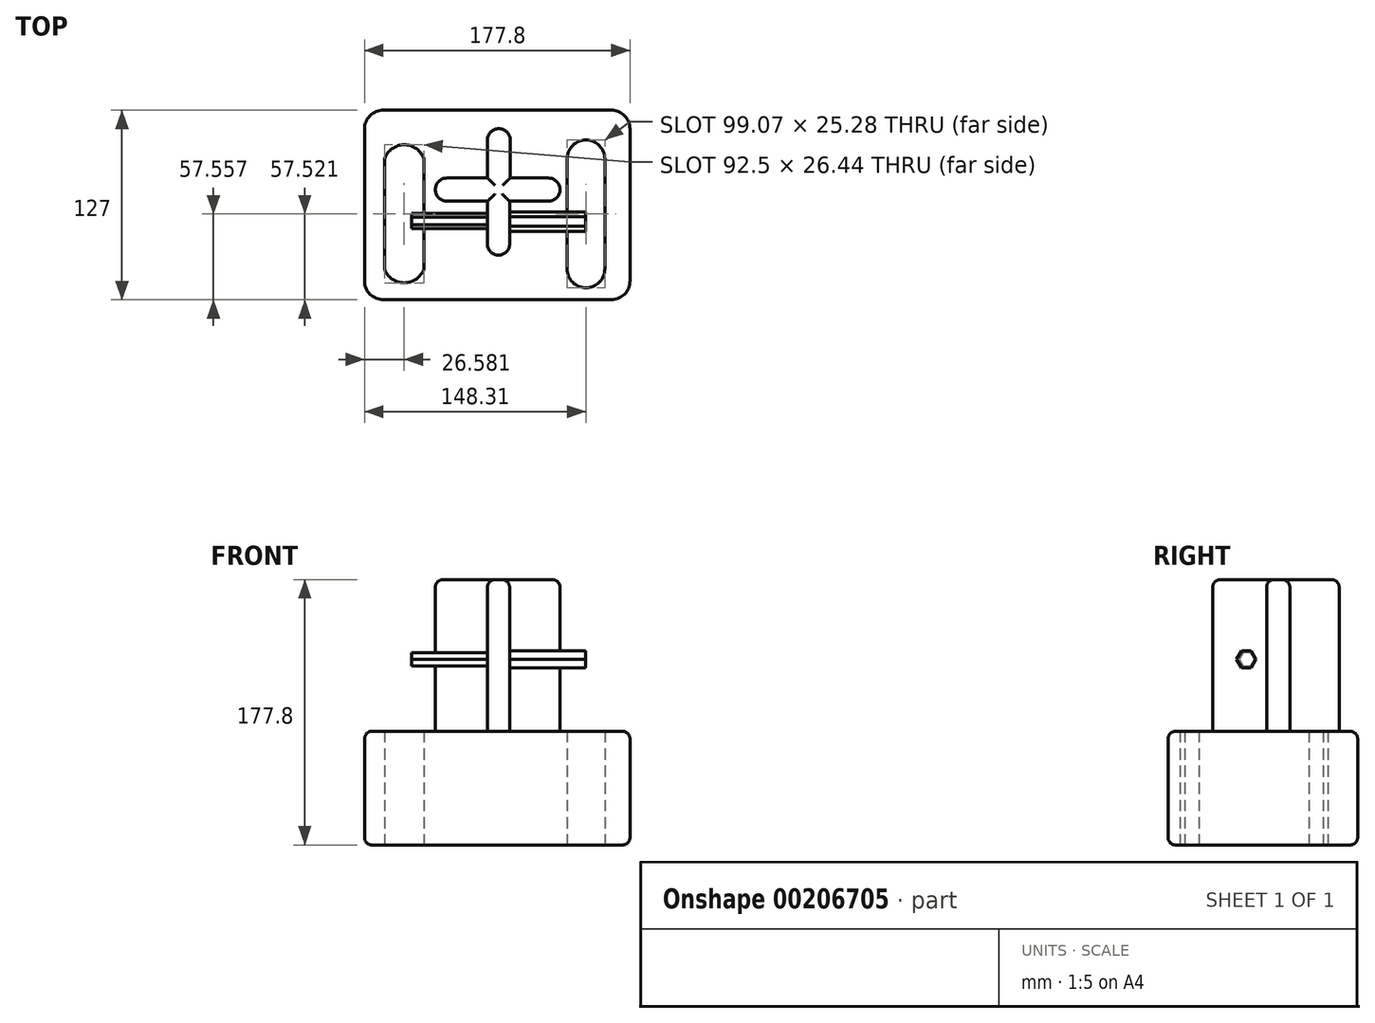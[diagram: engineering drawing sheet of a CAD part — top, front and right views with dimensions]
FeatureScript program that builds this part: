
annotation { "Feature Type Name" : "Feature", "Feature Type Description" : "" }
export const myFeature = defineFeature(function(context is Context, id is Id, definition is map)
    precondition{}
    {
        {
            var Q0;
            Q0=qCreatedBy(makeId("Top.planeOp"),FACE);
            var sketch = newSketch(context, id + "F0", { "sketchPlane" : qUnion([Q0])});
            skLineSegment(sketch, "E0", {"start": v(-97.17, 61.03) * mm, "end": v(-97.17, -65.97) * mm});
            skLineSegment(sketch, "E1", {"start": v(-97.17, -65.97) * mm, "end": v(80.63, -65.97) * mm});
            skLineSegment(sketch, "E2", {"start": v(80.63, -65.97) * mm, "end": v(80.63, 61.03) * mm});
            skLineSegment(sketch, "E3", {"start": v(80.63, 61.03) * mm, "end": v(-97.17, 61.03) * mm});
            skLineSegment(sketch, "E4", {"start": v(-83.8, 28.45) * mm, "end": v(-83.8, -45.35) * mm});
            skLineSegment(sketch, "E5", {"start": v(-57.37, 28.45) * mm, "end": v(-57.37, -45.35) * mm});
            skArc(sketch, "E6", {"start": v(-57.37, 28.45) * mm, "mid": v(-70.59, 37.84) * mm, "end": v(-83.8, 28.45) * mm});
            skArc(sketch, "E7", {"start": v(-83.8, -45.35) * mm, "mid": v(-70.59, -54.66) * mm, "end": v(-57.37, -45.35) * mm});
            skLineSegment(sketch, "E8", {"start": v(63.78, 28.45) * mm, "end": v(63.78, -45.35) * mm});
            skLineSegment(sketch, "E9", {"start": v(38.5, -45.35) * mm, "end": v(38.5, 28.45) * mm});
            skArc(sketch, "E10", {"start": v(63.78, 28.45) * mm, "mid": v(51.14, 41.09) * mm, "end": v(38.5, 28.45) * mm});
            skArc(sketch, "E11", {"start": v(38.5, -45.35) * mm, "mid": v(51.14, -57.98) * mm, "end": v(63.78, -45.35) * mm});
            skSolve(sketch);
        }
        {
            var Q0;
            Q0=makeQuery(id+"F0.imprint","IMPRINT",FACE,{"disambiguationData":[TD([[makeQuery(id+"F0.imprint","IMPRINT",EDGE,{"derivedFrom":sQuery(id+"F0.wireOp",EDGE,"E0")}),1.0]])]});
            extrude(context, id + "F1", {"entities" : qUnion([Q0]), "depth" : 76.2 * mm});
        }
        {
            var Q0;
            Q0=makeQuery(id+"F1.opExtrude","SWEPT_EDGE",EDGE,{"disambiguationData":[OSD([sQuery(id+"F0.wireOp",EDGE,"E2"),sQuery(id+"F0.wireOp",EDGE,"E3")])]});
            var Q1;
            Q1=makeQuery(id+"F1.opExtrude","SWEPT_EDGE",EDGE,{"disambiguationData":[OSD([sQuery(id+"F0.wireOp",EDGE,"E1"),sQuery(id+"F0.wireOp",EDGE,"E2")])]});
            var Q2;
            Q2=makeQuery(id+"F1.opExtrude","SWEPT_EDGE",EDGE,{"disambiguationData":[OSD([sQuery(id+"F0.wireOp",EDGE,"E0"),sQuery(id+"F0.wireOp",EDGE,"E3")])]});
            var Q3;
            Q3=makeQuery(id+"F1.opExtrude","SWEPT_EDGE",EDGE,{"disambiguationData":[OSD([sQuery(id+"F0.wireOp",EDGE,"E0"),sQuery(id+"F0.wireOp",EDGE,"E1")])]});
            fillet(context, id + "F2", {"entities" : qUnion([Q0, Q1, Q2, Q3]), "radius" : 12.7 * mm, "tangentPropagation" : true, "allowEdgeOverflow" : false});
        }
        {
            var Q0;
            Q0=makeQuery(id+"F1.opExtrude","CAP_FACE",FACE,{"disambiguationData":[OSD([sQuery(id+"F0.wireOp",EDGE,"E0"),sQuery(id+"F0.wireOp",EDGE,"E1"),sQuery(id+"F0.wireOp",EDGE,"E2"),sQuery(id+"F0.wireOp",EDGE,"E3"),sQuery(id+"F0.wireOp",EDGE,"E4"),sQuery(id+"F0.wireOp",EDGE,"E5"),sQuery(id+"F0.wireOp",EDGE,"E6"),sQuery(id+"F0.wireOp",EDGE,"E7"),sQuery(id+"F0.wireOp",EDGE,"E8"),sQuery(id+"F0.wireOp",EDGE,"E9"),sQuery(id+"F0.wireOp",EDGE,"E10"),sQuery(id+"F0.wireOp",EDGE,"E11")])],"isStart":false});
            var sketch = newSketch(context, id + "F3", { "sketchPlane" : qUnion([Q0])});
            skLineSegment(sketch, "E12", {"start": v(-14.84, 41) * mm, "end": v(-14.84, 15.58) * mm});
            skLineSegment(sketch, "E13", {"start": v(0.43, 41) * mm, "end": v(0.43, 15.58) * mm});
            skArc(sketch, "E14", {"start": v(0.43, 41) * mm, "mid": v(-7.2, 48.63) * mm, "end": v(-14.84, 41) * mm});
            skLineSegment(sketch, "E15", {"start": v(-14.84, 15.58) * mm, "end": v(-41.93, 15.58) * mm});
            skLineSegment(sketch, "E16", {"start": v(-41.93, 0) * mm, "end": v(-14.84, 0) * mm});
            skLineSegment(sketch, "E17", {"start": v(-14.84, 0) * mm, "end": v(-14.84, -28.67) * mm});
            skLineSegment(sketch, "E18", {"start": v(0, -28.67) * mm, "end": v(0, 0) * mm});
            skLineSegment(sketch, "E19", {"start": v(0, 0) * mm, "end": v(25.96, 0) * mm});
            skLineSegment(sketch, "E20", {"start": v(25.96, 15.58) * mm, "end": v(0.43, 15.58) * mm});
            skArc(sketch, "E21", {"start": v(-41.93, 15.58) * mm, "mid": v(-49.72, 7.8) * mm, "end": v(-41.93, 0) * mm});
            skArc(sketch, "E22", {"start": v(25.96, 0) * mm, "mid": v(33.75, 7.8) * mm, "end": v(25.96, 15.58) * mm});
            skArc(sketch, "E23", {"start": v(-14.84, -28.67) * mm, "mid": v(-7.42, -36.09) * mm, "end": v(0, -28.67) * mm});
            skSolve(sketch);
        }
        {
            var Q0;
            Q0=makeQuery(id+"F3.imprint","IMPRINT",FACE,{"disambiguationData":[TD([[makeQuery(id+"F3.imprint","IMPRINT",EDGE,{"derivedFrom":sQuery(id+"F3.wireOp",EDGE,"E12")}),1.0]])]});
            extrude(context, id + "F4", {"entities" : qUnion([Q0]), "operationType" : NewBodyOperationType.ADD, "depth" : 101.6 * mm});
        }
        {
            var Q0;
            Q0=makeQuery(id+"F4.opExtrude","SWEPT_FACE",FACE,{"disambiguationData":[OSD([sQuery(id+"F3.wireOp",EDGE,"E18")])]});
            var sketch = newSketch(context, id + "F5", { "sketchPlane" : qUnion([Q0])});
            skCircle(sketch, "E24.cCircle", {"center": v(-13.55, 124.42) * mm, "radius": 5.65 * mm, "construction": true});
            skLineSegment(sketch, "E24.0", {"start": v(-10.29, 118.77) * mm, "end": v(-16.8, 118.77) * mm});
            skLineSegment(sketch, "E24.1", {"start": v(-16.8, 118.77) * mm, "end": v(-20.07, 124.42) * mm});
            skLineSegment(sketch, "E24.2", {"start": v(-20.07, 124.42) * mm, "end": v(-16.8, 130.07) * mm});
            skLineSegment(sketch, "E24.3", {"start": v(-16.8, 130.07) * mm, "end": v(-10.29, 130.07) * mm});
            skLineSegment(sketch, "E24.4", {"start": v(-10.29, 130.07) * mm, "end": v(-7.03, 124.42) * mm});
            skLineSegment(sketch, "E24.5", {"start": v(-7.03, 124.42) * mm, "end": v(-10.29, 118.77) * mm});
            skPoint(sketch, "E24.0.midPoint", {"position": v(-13.55, 118.77) * mm});
            skSolve(sketch);
        }
        {
            var Q0;
            Q0=makeQuery(id+"F5.imprint","IMPRINT",FACE,{"disambiguationData":[TD([[makeQuery(id+"F5.imprint","IMPRINT",EDGE,{"derivedFrom":sQuery(id+"F5.wireOp",EDGE,"E24.0")}),-1.0]])]});
            extrude(context, id + "F6", {"entities" : qUnion([Q0]), "operationType" : NewBodyOperationType.ADD, "depth" : 50.8 * mm});
        }
        {
            var Q0;
            Q0=makeQuery(id+"F4.opExtrude","SWEPT_FACE",FACE,{"disambiguationData":[OSD([sQuery(id+"F3.wireOp",EDGE,"E17")])]});
            var sketch = newSketch(context, id + "F7", { "sketchPlane" : qUnion([Q0])});
            skCircle(sketch, "E25.cCircle", {"center": v(13.26, 124.33) * mm, "radius": 4.44 * mm, "construction": true});
            skLineSegment(sketch, "E25.0", {"start": v(10.7, 128.77) * mm, "end": v(15.83, 128.77) * mm});
            skLineSegment(sketch, "E25.1", {"start": v(15.83, 128.77) * mm, "end": v(18.39, 124.33) * mm});
            skLineSegment(sketch, "E25.2", {"start": v(18.39, 124.33) * mm, "end": v(15.83, 119.9) * mm});
            skLineSegment(sketch, "E25.3", {"start": v(15.83, 119.9) * mm, "end": v(10.7, 119.9) * mm});
            skLineSegment(sketch, "E25.4", {"start": v(10.7, 119.9) * mm, "end": v(8.14, 124.33) * mm});
            skLineSegment(sketch, "E25.5", {"start": v(8.14, 124.33) * mm, "end": v(10.7, 128.77) * mm});
            skPoint(sketch, "E25.0.midPoint", {"position": v(13.26, 128.77) * mm});
            skSolve(sketch);
        }
        {
            var Q0;
            Q0=makeQuery(id+"F7.imprint","IMPRINT",FACE,{"disambiguationData":[TD([[makeQuery(id+"F7.imprint","IMPRINT",EDGE,{"derivedFrom":sQuery(id+"F7.wireOp",EDGE,"E25.0")}),-1.0]])]});
            extrude(context, id + "F8", {"entities" : qUnion([Q0]), "operationType" : NewBodyOperationType.ADD, "depth" : 50.8 * mm});
        }
        {
            var Q0;
            Q0=makeQuery(id+"F4.opExtrude","CAP_FACE",FACE,{"disambiguationData":[OSD([sQuery(id+"F3.wireOp",EDGE,"E12"),sQuery(id+"F3.wireOp",EDGE,"E13"),sQuery(id+"F3.wireOp",EDGE,"E14"),sQuery(id+"F3.wireOp",EDGE,"E15"),sQuery(id+"F3.wireOp",EDGE,"E16"),sQuery(id+"F3.wireOp",EDGE,"E17"),sQuery(id+"F3.wireOp",EDGE,"E18"),sQuery(id+"F3.wireOp",EDGE,"E19"),sQuery(id+"F3.wireOp",EDGE,"E20"),sQuery(id+"F3.wireOp",EDGE,"E21"),sQuery(id+"F3.wireOp",EDGE,"E22"),sQuery(id+"F3.wireOp",EDGE,"E23")])],"isStart":false});
            fillet(context, id + "F9", {"entities" : qUnion([Q0]), "radius" : 5.08 * mm, "tangentPropagation" : true, "allowEdgeOverflow" : false});
        }
        {
            var Q0;
            Q0=makeQuery(id+"F1.opExtrude","SWEPT_FACE",FACE,{"disambiguationData":[OSD([sQuery(id+"F0.wireOp",EDGE,"E0")])]});
            fillet(context, id + "F10", {"entities" : qUnion([Q0]), "radius" : 5.08 * mm, "tangentPropagation" : true, "allowEdgeOverflow" : false});
        }
    });
